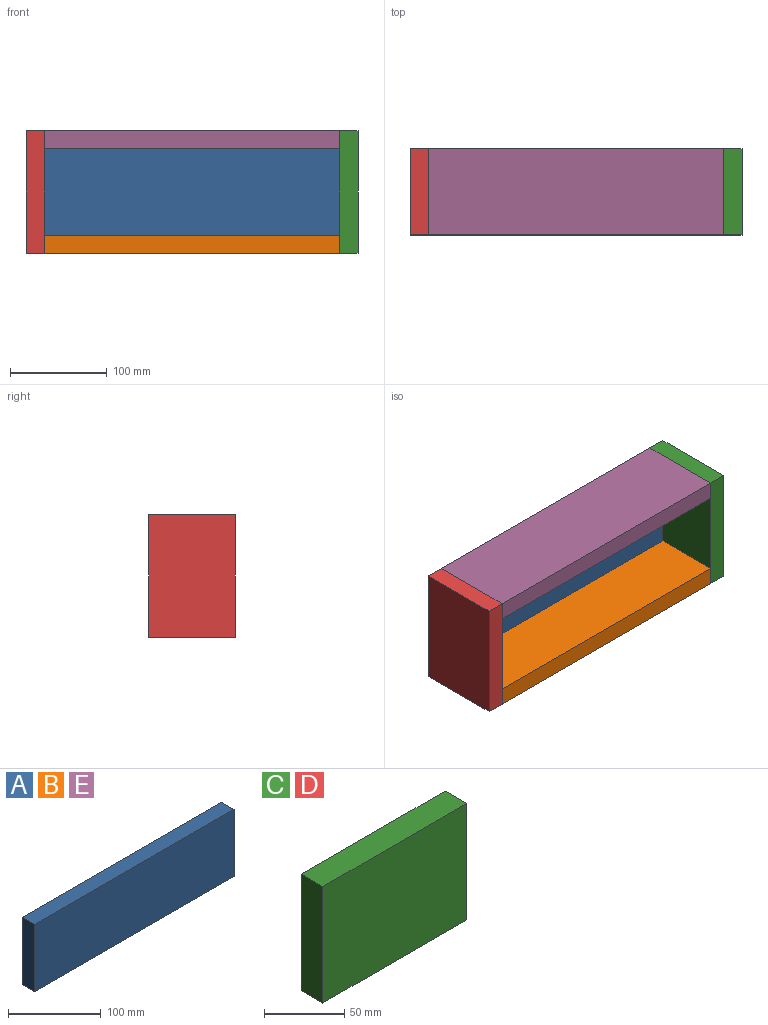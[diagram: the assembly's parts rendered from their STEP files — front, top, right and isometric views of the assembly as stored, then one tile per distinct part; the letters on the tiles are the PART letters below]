
ASSEMBLY  parts=5 mates=11
PART A: 6 faces, bbox 304.8x19.1x88.9 mm
  f0: plane 88.9x19.05mm, normal (-1,0,0), area 1693.5mm2, adj f1,f3,f4,f5
  f1: plane 304.8x19.05mm, normal (0,0,-1), area 5806.4mm2, adj f0,f2,f4,f5
  f2: plane 88.9x19.05mm, normal (1,0,0), area 1693.5mm2, adj f1,f3,f4,f5
  f3: plane 304.8x19.05mm, normal (0,0,1), area 5806.4mm2, adj f0,f2,f4,f5
  f4: plane 304.8x88.9mm, normal (0,-1,0), area 27096.7mm2, adj f0,f1,f2,f3
  f5: plane 304.8x88.9mm, normal (0,1,0), area 27096.7mm2, adj f0,f1,f2,f3
PART B: same geometry as A
PART C: 6 faces, bbox 127x19.1x88.9 mm
  f0: plane 127x19.05mm, normal (0,0,1), area 2419.3mm2, adj f1,f3,f4,f5
  f1: plane 88.9x19.05mm, normal (-1,0,0), area 1693.5mm2, adj f0,f2,f4,f5
  f2: plane 127x19.05mm, normal (0,0,-1), area 2419.3mm2, adj f1,f3,f4,f5
  f3: plane 88.9x19.05mm, normal (1,0,0), area 1693.5mm2, adj f0,f2,f4,f5
  f4: plane 127x88.9mm, normal (0,-1,0), area 11290.3mm2, adj f0,f1,f2,f3
  f5: plane 127x88.9mm, normal (0,1,0), area 11290.3mm2, adj f0,f1,f2,f3
PART D: same geometry as C
PART E: same geometry as A
PLACE A t=(0,0,53.97)mm fixed
PLACE B rot(axis=(-1,0,0),90deg) t=(0,-88.9,34.92)mm
PLACE C rot(axis=(0.58,0.58,-0.58),120deg) t=(323.85,-122.65,161.92)mm
PLACE D rot(axis=(0.58,-0.58,0.58),120deg) t=(-19.05,-122.65,34.92)mm
PLACE E rot(axis=(1,0,0),90deg) t=(0,0,161.92)mm
MATE planar D.f4 <-> A.f0  axis (1,0,0) through (0,-44.45,98.42)mm
MATE planar A.f5 <-> E.f1  axis (0,1,0) through (152.4,0,98.42)mm
MATE planar C.f2 <-> A.f5  axis (0,1,0) through (304.8,0,98.42)mm
MATE planar B.f4 <-> A.f1  axis (0,0,1) through (152.4,-44.45,53.97)mm
MATE planar E.f2 <-> A.f2  axis (1,0,0) through (304.8,0,152.4)mm
MATE planar C.f4 <-> A.f2  axis (-1,0,0) through (304.8,-88.9,98.42)mm
MATE planar B.f2 <-> A.f2  axis (1,0,0) through (304.8,-44.45,53.97)mm
MATE planar B.f3 <-> A.f5  axis (0,1,0) through (304.8,0,44.45)mm
MATE planar D.f2 <-> A.f5  axis (0,1,0) through (-9.53,0,98.42)mm
MATE planar E.f4 <-> A.f3  axis (0,0,-1) through (152.4,-44.45,142.87)mm
MATE planar B.f5 <-> D.f1  axis (0,0,-1) through (152.4,-44.45,34.92)mm
